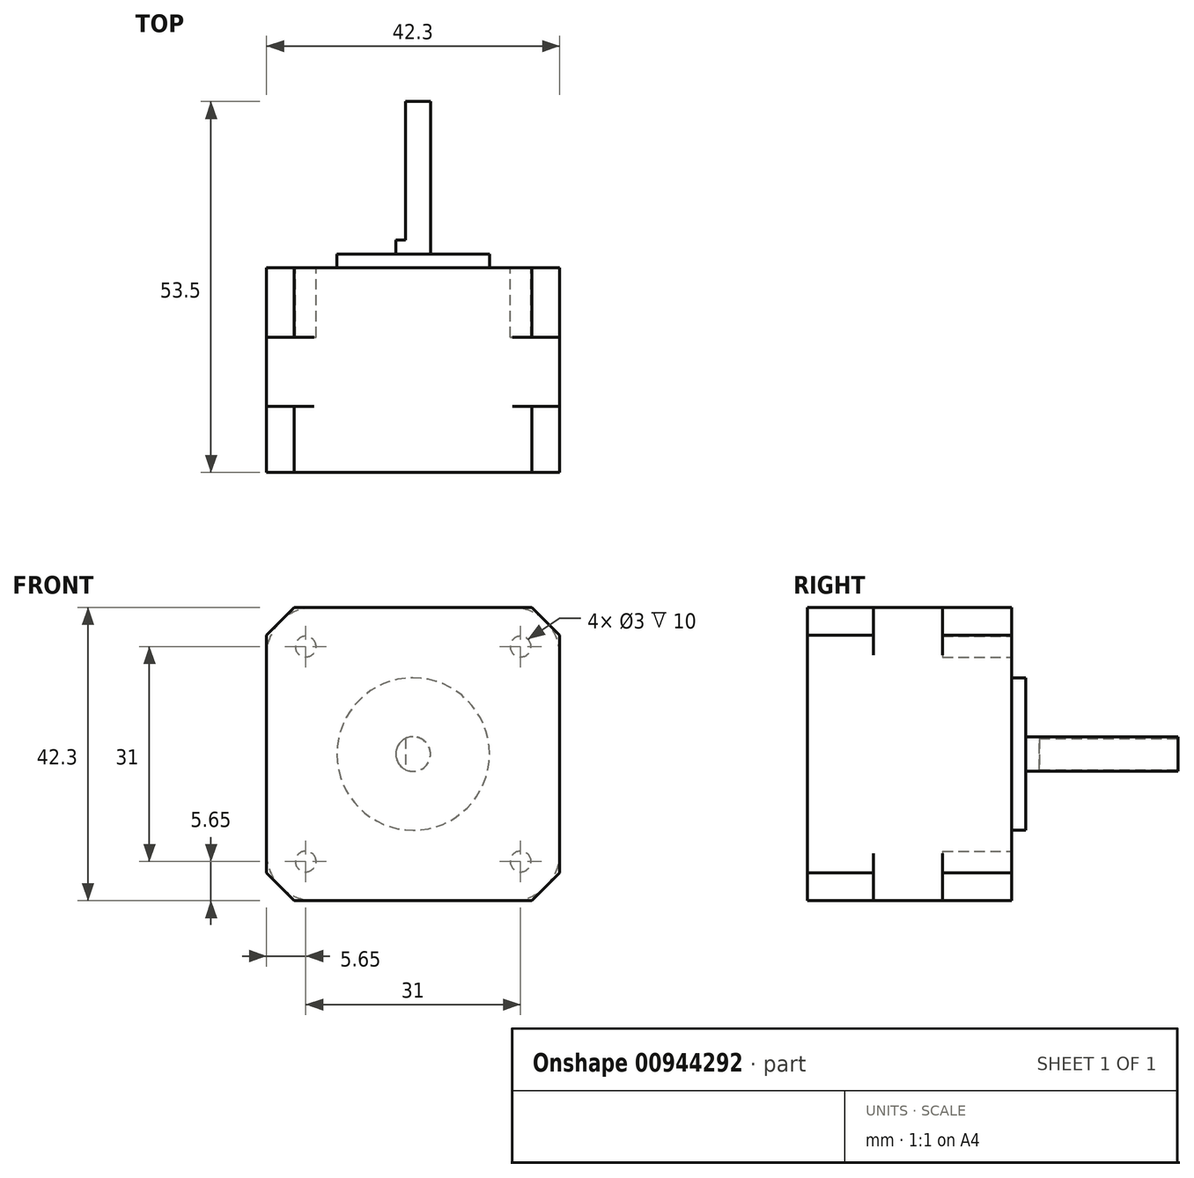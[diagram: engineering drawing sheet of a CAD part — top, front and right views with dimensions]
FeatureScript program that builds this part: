
annotation { "Feature Type Name" : "Feature", "Feature Type Description" : "" }
export const myFeature = defineFeature(function(context is Context, id is Id, definition is map)
    precondition{}
    {
        {
            var Q0;
            Q0=qCreatedBy(makeId("Front.planeOp"),FACE);
            var sketch = newSketch(context, id + "F0", { "sketchPlane" : qUnion([Q0])});
            skLineSegment(sketch, "E0.bottom", {"start": v(21.15, 21.15) * mm, "end": v(-21.15, 21.15) * mm});
            skLineSegment(sketch, "E0.top", {"start": v(21.15, -21.15) * mm, "end": v(-21.15, -21.15) * mm});
            skLineSegment(sketch, "E0.left", {"start": v(21.15, 21.15) * mm, "end": v(21.15, -21.15) * mm});
            skLineSegment(sketch, "E0.right", {"start": v(-21.15, 21.15) * mm, "end": v(-21.15, -21.15) * mm});
            skPoint(sketch, "E0.middle", {"position": v(0, 0) * mm});
            skPoint(sketch, "E1.visualSharp", {"position": v(-21.15, 21.15) * mm});
            skPoint(sketch, "E2.orphan", {"position": v(21.15, 21.15) * mm});
            skPoint(sketch, "E3.orphan", {"position": v(21.15, -21.15) * mm});
            skPoint(sketch, "E4.orphan", {"position": v(-21.15, -21.15) * mm});
            skSolve(sketch);
        }
        {
            var Q0;
            Q0=makeQuery(id+"F0.imprint","IMPRINT",FACE,{"disambiguationData":[TD([[makeQuery(id+"F0.imprint","IMPRINT",EDGE,{"derivedFrom":sQuery(id+"F0.wireOp",EDGE,"E0.bottom")}),1.0]])]});
            extrude(context, id + "F1", {"entities" : qUnion([Q0]), "depth" : 29.5 * mm, "offsetDistance" : 25 * mm});
        }
        {
            var Q0;
            Q0=makeQuery(id+"F1.opExtrude","CAP_FACE",FACE,{"disambiguationData":[OSD([sQuery(id+"F0.wireOp",EDGE,"E0.bottom"),sQuery(id+"F0.wireOp",EDGE,"E0.top"),sQuery(id+"F0.wireOp",EDGE,"E0.left"),sQuery(id+"F0.wireOp",EDGE,"E0.right"),sQuery(id+"F0.wireOp",EDGE,"Xe1pNUPd-5NHr-yC4v-04eJ-njersvvzofgt"),sQuery(id+"F0.wireOp",EDGE,"3830abb2-49cd-4b53-8be5-f5c9399e15470.MirrorC"),sQuery(id+"F0.wireOp",EDGE,"f7871d61-49dc-4b65-b8a3-a071d65dc2940.MirrorC"),sQuery(id+"F0.wireOp",EDGE,"5f0c8ad3-0e0d-44d6-be3f-279486d6b9530.MirrorC"),sQuery(id+"F0.wireOp",EDGE,"E1.filletArc"),sQuery(id+"F0.wireOp",EDGE,"bb470a36-2f72-4c16-97b8-b32c393a97940.MirrorCS"),sQuery(id+"F0.wireOp",EDGE,"2c940c82-93c7-4399-86c2-3b0c11c1d09e0.MirrorCS"),sQuery(id+"F0.wireOp",EDGE,"18518c19-3f0e-4304-99dd-ba4c207d6b000.MirrorCS")])],"isStart":true});
            var sketch = newSketch(context, id + "F2", { "sketchPlane" : qUnion([Q0])});
            skCircle(sketch, "E5", {"center": v(0, 0) * mm, "radius": 11 * mm});
            skSolve(sketch);
        }
        {
            var Q0;
            Q0=makeQuery(id+"F2.imprint","IMPRINT",FACE,{"disambiguationData":[TD([[makeQuery(id+"F2.imprint","IMPRINT",EDGE,{"derivedFrom":sQuery(id+"F2.wireOp",EDGE,"E5")}),1.0]])]});
            extrude(context, id + "F3", {"entities" : qUnion([Q0]), "operationType" : NewBodyOperationType.ADD, "depth" : 2 * mm, "offsetDistance" : 25 * mm});
        }
        {
            var Q0;
            Q0=makeQuery(id+"F3.opExtrude","CAP_FACE",FACE,{"disambiguationData":[OSD([sQuery(id+"F2.wireOp",EDGE,"E5")])],"isStart":false});
            var sketch = newSketch(context, id + "F4", { "sketchPlane" : qUnion([Q0])});
            skCircle(sketch, "E6", {"center": v(0, 0) * mm, "radius": 2.5 * mm});
            skSolve(sketch);
        }
        {
            var Q0;
            Q0=makeQuery(id+"F4.imprint","IMPRINT",FACE,{"disambiguationData":[TD([[makeQuery(id+"F4.imprint","IMPRINT",EDGE,{"derivedFrom":sQuery(id+"F4.wireOp",EDGE,"E6")}),1.0]])]});
            extrude(context, id + "F5", {"entities" : qUnion([Q0]), "operationType" : NewBodyOperationType.ADD, "depth" : 22 * mm, "offsetDistance" : 25 * mm});
        }
        {
            var Q0;
            Q0=makeQuery(id+"F5.opExtrude","CAP_FACE",FACE,{"disambiguationData":[OSD([sQuery(id+"F4.wireOp",EDGE,"E6")])],"isStart":false});
            var sketch = newSketch(context, id + "F6", { "sketchPlane" : qUnion([Q0])});
            skLineSegment(sketch, "E7", {"start": v(1.09, 2.25) * mm, "end": v(1.09, -2.25) * mm});
            skSolve(sketch);
        }
        {
            var Q0;
            {var subQ0=sQuery(id+"F6.wireOp",EDGE,"E7");Q0=makeQuery(id+"F6.imprint","IMPRINT",FACE,{"disambiguationData":[TD([[makeQuery(id+"F6.imprint","IMPRINT",EDGE,{"derivedFrom":subQ0}),1.0]])]});}
            extrude(context, id + "F7", {"entities" : qUnion([Q0]), "operationType" : NewBodyOperationType.REMOVE, "oppositeDirection" : true, "depth" : 20 * mm, "offsetDistance" : 25 * mm});
        }
        {
            var Q0;
            Q0=makeQuery(id+"F1.opExtrude","SWEPT_EDGE",EDGE,{"disambiguationData":[OSD([sQuery(id+"F0.wireOp",EDGE,"E0.bottom"),sQuery(id+"F0.wireOp",EDGE,"E0.right")])]});
            var Q1;
            Q1=makeQuery(id+"F1.opExtrude","SWEPT_EDGE",EDGE,{"disambiguationData":[OSD([sQuery(id+"F0.wireOp",EDGE,"E0.top"),sQuery(id+"F0.wireOp",EDGE,"E0.right")])]});
            var Q2;
            Q2=makeQuery(id+"F1.opExtrude","SWEPT_EDGE",EDGE,{"disambiguationData":[OSD([sQuery(id+"F0.wireOp",EDGE,"E0.top"),sQuery(id+"F0.wireOp",EDGE,"E0.left")])]});
            var Q3;
            Q3=makeQuery(id+"F1.opExtrude","SWEPT_EDGE",EDGE,{"disambiguationData":[OSD([sQuery(id+"F0.wireOp",EDGE,"E0.bottom"),sQuery(id+"F0.wireOp",EDGE,"E0.left")])]});
            chamfer(context, id + "F8", {"entities" : qUnion([Q0, Q1, Q2, Q3]), "width" : 4 * mm, "tangentPropagation" : true});
        }
        {
            var Q0;
            Q0=qCreatedBy(makeId("Front.planeOp"),FACE);
            cPlane(context, id + "F9", {"entities" : qUnion([Q0]), "cplaneType" : CPlaneType.OFFSET, "offset" : 15 * mm, "width" : 150 * mm, "height" : 150 * mm});
        }
        {
            var Q0;
            Q0=qCreatedBy(id+"F9.planeOp",FACE);
            var sketch = newSketch(context, id + "F10", { "sketchPlane" : qUnion([Q0])});
            skLineSegment(sketch, "E8", {"start": v(21.15, 0) * mm, "end": v(21.15, 14.32) * mm});
            skLineSegment(sketch, "E9", {"start": v(0, 21.15) * mm, "end": v(14.32, 21.15) * mm});
            skArc(sketch, "E10", {"start": v(21.15, 14.32) * mm, "mid": v(19.15, 19.15) * mm, "end": v(14.32, 21.15) * mm});
            skLineSegment(sketch, "E11", {"start": v(21.15, 14.32) * mm, "end": v(21.15, 21.15) * mm});
            skLineSegment(sketch, "E12", {"start": v(21.15, 21.15) * mm, "end": v(14.32, 21.15) * mm});
            skArc(sketch, "E13.MirrorCS", {"start": v(-21.15, 14.32) * mm, "mid": v(-19.15, 19.15) * mm, "end": v(-14.32, 21.15) * mm});
            skLineSegment(sketch, "E14.MirrorCS", {"start": v(-21.15, 21.15) * mm, "end": v(-14.32, 21.15) * mm});
            skLineSegment(sketch, "E15.MirrorCS", {"start": v(-21.15, 14.32) * mm, "end": v(-21.15, 21.15) * mm});
            skArc(sketch, "E16.MirrorCS", {"start": v(21.15, -14.32) * mm, "mid": v(19.15, -19.15) * mm, "end": v(14.32, -21.15) * mm});
            skLineSegment(sketch, "E17.MirrorCS", {"start": v(21.15, -14.32) * mm, "end": v(21.15, -21.15) * mm});
            skLineSegment(sketch, "E18.MirrorCS", {"start": v(21.15, -21.15) * mm, "end": v(14.32, -21.15) * mm});
            skArc(sketch, "E19.MirrorCS", {"start": v(-21.15, -14.32) * mm, "mid": v(-19.15, -19.15) * mm, "end": v(-14.32, -21.15) * mm});
            skLineSegment(sketch, "E20.MirrorCS", {"start": v(-21.15, -21.15) * mm, "end": v(-14.32, -21.15) * mm});
            skLineSegment(sketch, "E21.MirrorCS", {"start": v(-21.15, -14.32) * mm, "end": v(-21.15, -21.15) * mm});
            skSolve(sketch);
        }
        {
            var Q0;
            Q0 = qSketchRegion(id + "F10", true);
            extrude(context, id + "F11", {"entities" : qUnion([Q0]), "operationType" : NewBodyOperationType.REMOVE, "depth" : 10 * mm, "offsetDistance" : 25 * mm, "symmetric" : true});
        }
        {
            var Q0;
            Q0=makeQuery(id+"F1.opExtrude","CAP_FACE",FACE,{"disambiguationData":[OSD([sQuery(id+"F0.wireOp",EDGE,"E0.bottom"),sQuery(id+"F0.wireOp",EDGE,"E0.top"),sQuery(id+"F0.wireOp",EDGE,"E0.left"),sQuery(id+"F0.wireOp",EDGE,"E0.right")])],"isStart":true});
            var sketch = newSketch(context, id + "F12", { "sketchPlane" : qUnion([Q0])});
            skCircle(sketch, "E22", {"center": v(-15.5, 15.5) * mm, "radius": 1.5 * mm});
            skCircle(sketch, "E23.MirrorC", {"center": v(15.5, 15.5) * mm, "radius": 1.5 * mm});
            skCircle(sketch, "E24.MirrorC", {"center": v(-15.5, -15.5) * mm, "radius": 1.5 * mm});
            skCircle(sketch, "E25.MirrorC", {"center": v(15.5, -15.5) * mm, "radius": 1.5 * mm});
            skSolve(sketch);
        }
        {
            var Q0;
            Q0 = qSketchRegion(id + "F12", true);
            extrude(context, id + "F13", {"entities" : qUnion([Q0]), "operationType" : NewBodyOperationType.REMOVE, "oppositeDirection" : true, "depth" : 10 * mm, "offsetDistance" : 25 * mm});
        }
    });
